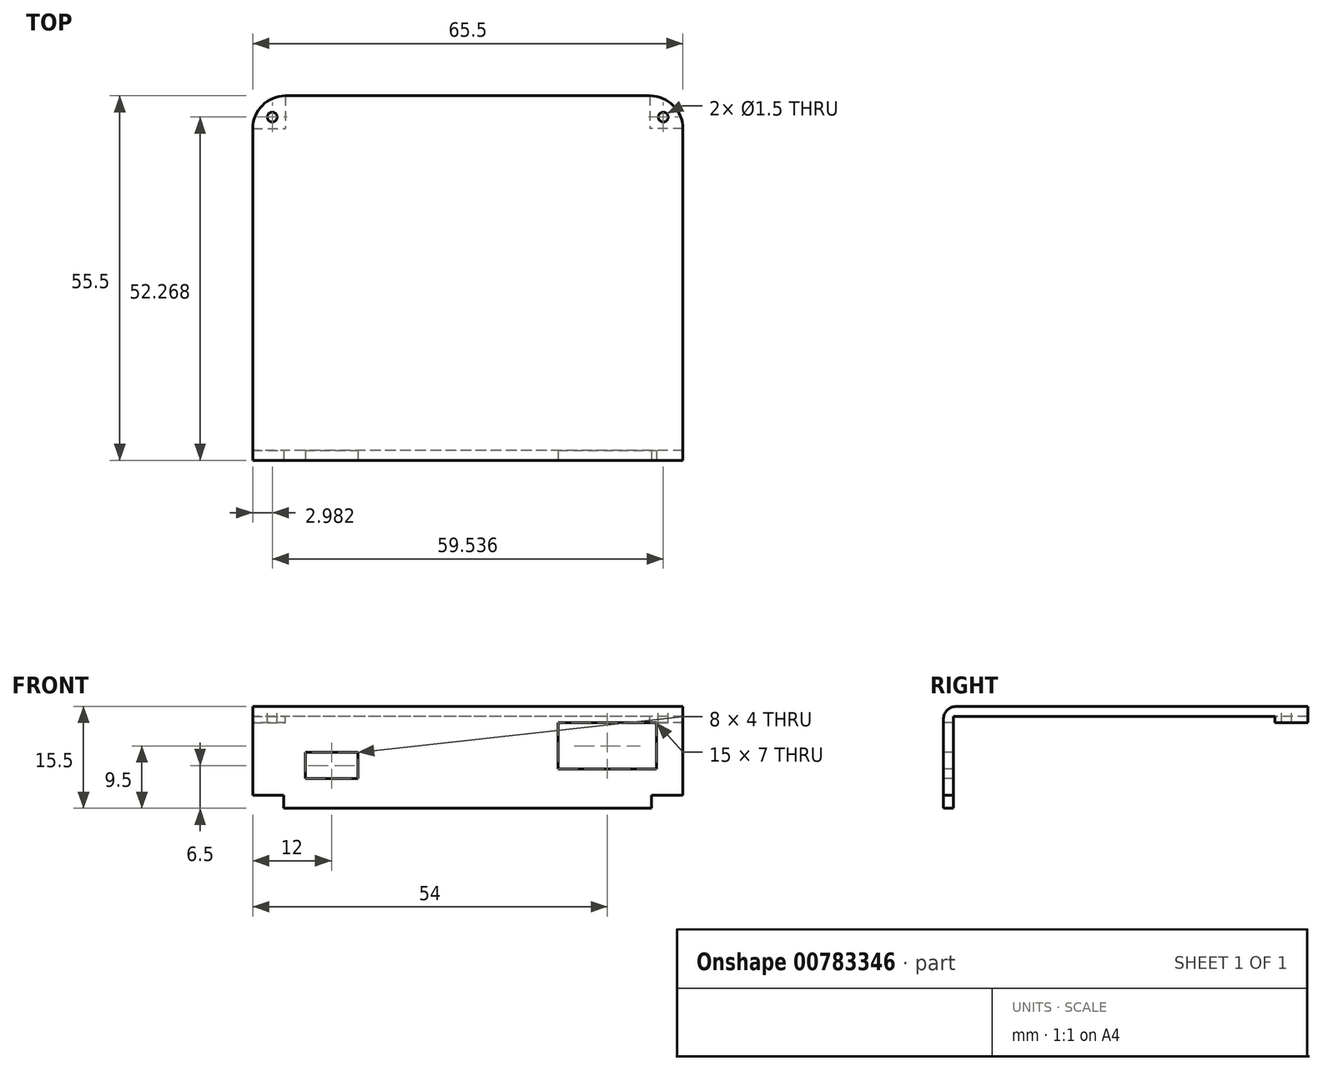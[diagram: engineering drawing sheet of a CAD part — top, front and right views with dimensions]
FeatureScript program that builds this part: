
annotation { "Feature Type Name" : "Feature", "Feature Type Description" : "" }
export const myFeature = defineFeature(function(context is Context, id is Id, definition is map)
    precondition{}
    {
        {
            var Q0;
            Q0=qCreatedBy(makeId("Right.planeOp"),FACE);
            var sketch = newSketch(context, id + "F0", { "sketchPlane" : qUnion([Q0])});
            skLineSegment(sketch, "E0", {"start": v(-34.56, 0) * mm, "end": v(-34.56, 14) * mm});
            skLineSegment(sketch, "E1", {"start": v(-34.56, 14) * mm, "end": v(19.44, 14) * mm});
            skLineSegment(sketch, "E2.0", {"start": v(-34.06, 15.5) * mm, "end": v(19.44, 15.5) * mm});
            skLineSegment(sketch, "E2.1", {"start": v(-36.06, 0) * mm, "end": v(-36.06, 13.5) * mm});
            skLineSegment(sketch, "E3", {"start": v(19.44, 14) * mm, "end": v(19.44, 30.41) * mm, "construction": true});
            skLineSegment(sketch, "E4", {"start": v(-36.06, 0) * mm, "end": v(-34.56, 0) * mm});
            skLineSegment(sketch, "E5", {"start": v(19.44, 15.5) * mm, "end": v(19.44, 14) * mm});
            skPoint(sketch, "E6.visualSharp", {"position": v(-36.06, 15.5) * mm});
            skArc(sketch, "E6.filletArc", {"start": v(-34.06, 15.5) * mm, "mid": v(-35.47, 14.91) * mm, "end": v(-36.06, 13.5) * mm});
            skSolve(sketch);
        }
        {
            var Q0;
            Q0=makeQuery(id+"F0.imprint","IMPRINT",FACE,{"disambiguationData":[TD([[makeQuery(id+"F0.imprint","IMPRINT",EDGE,{"derivedFrom":sQuery(id+"F0.wireOp",EDGE,"E0")}),1.0]])]});
            extrude(context, id + "F1", {"entities" : qUnion([Q0]), "depth" : 65.5 * mm, "offsetDistance" : 25 * mm});
        }
        {
            var Q0;
            Q0=makeQuery(id+"F1.opExtrude","CAP_EDGE",EDGE,{"disambiguationData":[OSD([sQuery(id+"F0.wireOp",EDGE,"E5")])],"isStart":false});
            var Q1;
            Q1=makeQuery(id+"F1.opExtrude","CAP_EDGE",EDGE,{"disambiguationData":[OSD([sQuery(id+"F0.wireOp",EDGE,"E5")])],"isStart":true});
            fillet(context, id + "F2", {"entities" : qUnion([Q0, Q1]), "radius" : 5 * mm, "tangentPropagation" : true, "allowEdgeOverflow" : false});
        }
        {
            var Q0;
            Q0=makeQuery(id+"F1.opExtrude","SWEPT_FACE",FACE,{"disambiguationData":[OSD([sQuery(id+"F0.wireOp",EDGE,"E1")])]});
            var sketch = newSketch(context, id + "F3", { "sketchPlane" : qUnion([Q0])});
            skLineSegment(sketch, "E7", {"start": v(188.31, 27.66) * mm, "end": v(188.31, -38.17) * mm, "construction": true});
            skPoint(sketch, "E8.visualSharp", {"position": v(65.75, -17.94) * mm});
            skPoint(sketch, "E9.orphan", {"position": v(63.75, -17.94) * mm});
            skLineSegment(sketch, "E10", {"start": v(32.75, 36.06) * mm, "end": v(32.75, 48.39) * mm, "construction": true});
            skPoint(sketch, "E10.startSnap0", {"position": v(32.75, 34.56) * mm});
            skPoint(sketch, "E11", {"position": v(62.52, -14.7) * mm});
            skLineSegment(sketch, "E12", {"start": v(65.5, -14.44) * mm, "end": v(60.5, -14.44) * mm});
            skLineSegment(sketch, "E13", {"start": v(60.5, -19.44) * mm, "end": v(60.5, -14.44) * mm});
            skArc(sketch, "E14", {"start": v(60.5, -19.44) * mm, "mid": v(64.04, -17.98) * mm, "end": v(65.5, -14.44) * mm});
            skLineSegment(sketch, "E15", {"start": v(2.98, -14.7) * mm, "end": v(2.98, -26.76) * mm, "construction": true});
            skLineSegment(sketch, "E16", {"start": v(2.98, -14.7) * mm, "end": v(-5.54, -14.7) * mm, "construction": true});
            skArc(sketch, "E17.MirrorCS", {"start": v(5, -19.44) * mm, "mid": v(1.46, -17.98) * mm, "end": v(0, -14.44) * mm});
            skPoint(sketch, "E18.MirrorP", {"position": v(-0.25, -17.94) * mm});
            skLineSegment(sketch, "E19.MirrorCS", {"start": v(5, -19.44) * mm, "end": v(5, -14.44) * mm});
            skPoint(sketch, "E20.MirrorP", {"position": v(1.75, -17.94) * mm});
            skPoint(sketch, "E21.MirrorP", {"position": v(2.98, -14.7) * mm});
            skLineSegment(sketch, "E22.MirrorCS", {"start": v(0, -14.44) * mm, "end": v(5, -14.44) * mm});
            skSolve(sketch);
        }
        {
            var Q0;
            Q0=makeQuery(id+"F3.imprint","IMPRINT",FACE,{"disambiguationData":[TD([[makeQuery(id+"F3.imprint","IMPRINT",EDGE,{"derivedFrom":sQuery(id+"F3.wireOp",EDGE,"E17.MirrorCS")}),1.0]])]});
            var Q1;
            Q1=makeQuery(id+"F3.imprint","IMPRINT",FACE,{"disambiguationData":[TD([[makeQuery(id+"F3.imprint","IMPRINT",EDGE,{"derivedFrom":sQuery(id+"F3.wireOp",EDGE,"E12")}),1.0]])]});
            extrude(context, id + "F4", {"entities" : qUnion([Q0, Q1]), "operationType" : NewBodyOperationType.ADD, "depth" : 1 * mm, "offsetDistance" : 25 * mm});
        }
        {
            var Q0;
            Q0=makeQuery(id+"F1.opExtrude","SWEPT_FACE",FACE,{"disambiguationData":[OSD([sQuery(id+"F0.wireOp",EDGE,"E2.0")])]});
            var sketch = newSketch(context, id + "F5", { "sketchPlane" : qUnion([Q0])});
            skLineSegment(sketch, "E23", {"start": v(2.98, 16.2) * mm, "end": v(2.98, 23.76) * mm, "construction": true});
            skLineSegment(sketch, "E24", {"start": v(62.52, 16.2) * mm, "end": v(62.52, 23.76) * mm, "construction": true});
            skPoint(sketch, "E25", {"position": v(2.98, 16.2) * mm});
            skPoint(sketch, "E26", {"position": v(62.52, 16.2) * mm});
            skSolve(sketch);
        }
        {
            var Q0;
            Q0=sQuery(id+"F5.wireOp",VERTEX,"E25");
            var Q1;
            Q1=sQuery(id+"F5.wireOp",VERTEX,"E26");
            var Q2;
            Q2=makeQuery(id+"F1.opExtrude","SWEPT_BODY",BODY,{"disambiguationData":[OSD([sQuery(id+"F0.wireOp",EDGE,"E0"),sQuery(id+"F0.wireOp",EDGE,"E1"),sQuery(id+"F0.wireOp",EDGE,"E2.0"),sQuery(id+"F0.wireOp",EDGE,"E2.1"),sQuery(id+"F0.wireOp",EDGE,"E4"),sQuery(id+"F0.wireOp",EDGE,"E5"),sQuery(id+"F0.wireOp",EDGE,"E6.filletArc")])]});
            hole(context, id + "F6", {"style" : HoleStyle.SIMPLE, "endStyle" : HoleEndStyle.BLIND, "holeDiameter" : 1.5 * mm, "majorDiameter" : 5 * mm, "holeDepth" : 5 * mm, "isTappedThrough" : true, "tappedDepth" : 12 * mm, "tapClearance" : 3, "startFromSketch" : true, "locations" : qUnion([Q0, Q1]), "scope" : qUnion([Q2])});
        }
        {
            var Q0;
            Q0=makeQuery(id+"F1.opExtrude","SWEPT_FACE",FACE,{"disambiguationData":[OSD([sQuery(id+"F0.wireOp",EDGE,"E2.1")])]});
            var sketch = newSketch(context, id + "F7", { "sketchPlane" : qUnion([Q0])});
            skLineSegment(sketch, "E27", {"start": v(8, 0) * mm, "end": v(8, 4) * mm, "construction": true});
            skLineSegment(sketch, "E28", {"start": v(0, 8) * mm, "end": v(8, 8) * mm, "construction": true});
            skLineSegment(sketch, "E29", {"start": v(61.5, 0) * mm, "end": v(61.5, 13) * mm, "construction": true});
            skLineSegment(sketch, "E30", {"start": v(65.5, 13) * mm, "end": v(61.5, 13) * mm, "construction": true});
            skLineSegment(sketch, "E31.bottom", {"start": v(46.5, 13) * mm, "end": v(61.5, 13) * mm});
            skLineSegment(sketch, "E31.top", {"start": v(46.5, 6) * mm, "end": v(61.5, 6) * mm});
            skLineSegment(sketch, "E31.left", {"start": v(46.5, 13) * mm, "end": v(46.5, 6) * mm});
            skLineSegment(sketch, "E31.right", {"start": v(61.5, 13) * mm, "end": v(61.5, 6) * mm});
            skLineSegment(sketch, "E32.bottom", {"start": v(8, 8.5) * mm, "end": v(16, 8.5) * mm});
            skLineSegment(sketch, "E32.top", {"start": v(8, 4.5) * mm, "end": v(16, 4.5) * mm});
            skLineSegment(sketch, "E32.left", {"start": v(8, 8.5) * mm, "end": v(8, 4) * mm});
            skLineSegment(sketch, "E32.right", {"start": v(16, 8.5) * mm, "end": v(16, 4.5) * mm});
            skLineSegment(sketch, "E33", {"start": v(32.75, 0) * mm, "end": v(32.75, -8.64) * mm, "construction": true});
            skLineSegment(sketch, "E34.bottom", {"start": v(0, 2) * mm, "end": v(4.75, 2) * mm});
            skLineSegment(sketch, "E34.top", {"start": v(0, 0) * mm, "end": v(4.75, 0) * mm});
            skLineSegment(sketch, "E34.left", {"start": v(0, 2) * mm, "end": v(0, 0) * mm});
            skLineSegment(sketch, "E34.right", {"start": v(4.75, 2) * mm, "end": v(4.75, 0) * mm});
            skLineSegment(sketch, "E35.MirrorCS", {"start": v(60.75, 2) * mm, "end": v(60.75, 0) * mm});
            skLineSegment(sketch, "E36.MirrorCS", {"start": v(65.5, 2) * mm, "end": v(60.75, 2) * mm});
            skLineSegment(sketch, "E37.MirrorCS", {"start": v(65.5, 2) * mm, "end": v(65.5, 0) * mm});
            skLineSegment(sketch, "E38.MirrorCS", {"start": v(65.5, 0) * mm, "end": v(60.75, 0) * mm});
            skLineSegment(sketch, "E39.trimOffspring", {"start": v(8, 4.5) * mm, "end": v(8, 8) * mm, "construction": true});
            skSolve(sketch);
        }
        {
            var Q0;
            Q0=makeQuery(id+"F7.imprint","IMPRINT",FACE,{"disambiguationData":[TD([[makeQuery(id+"F7.imprint","IMPRINT",EDGE,{"derivedFrom":sQuery(id+"F7.wireOp",EDGE,"E31.bottom")}),-1.0]])]});
            var Q1;
            Q1=makeQuery(id+"F7.imprint","IMPRINT",FACE,{"disambiguationData":[TD([[makeQuery(id+"F7.imprint","IMPRINT",EDGE,{"derivedFrom":sQuery(id+"F7.wireOp",EDGE,"E32.bottom")}),-1.0]])]});
            extrude(context, id + "F8", {"entities" : qUnion([Q0, Q1]), "operationType" : NewBodyOperationType.REMOVE, "oppositeDirection" : true, "depth" : 5 * mm, "offsetDistance" : 25 * mm});
        }
        {
            var Q0;
            Q0=makeQuery(id+"F7.imprint","IMPRINT",FACE,{"disambiguationData":[TD([[makeQuery(id+"F7.imprint","IMPRINT",EDGE,{"derivedFrom":sQuery(id+"F7.wireOp",EDGE,"E34.bottom")}),-1.0]])]});
            var Q1;
            Q1=makeQuery(id+"F7.imprint","IMPRINT",FACE,{"disambiguationData":[TD([[makeQuery(id+"F7.imprint","IMPRINT",EDGE,{"derivedFrom":sQuery(id+"F7.wireOp",EDGE,"E35.MirrorCS")}),1.0]])]});
            extrude(context, id + "F9", {"entities" : qUnion([Q0, Q1]), "operationType" : NewBodyOperationType.REMOVE, "oppositeDirection" : true, "depth" : 5 * mm, "offsetDistance" : 25 * mm});
        }
    });
